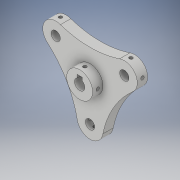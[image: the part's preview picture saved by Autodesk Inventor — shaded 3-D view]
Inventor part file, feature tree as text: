
AUTODESK INVENTOR PART (.ipt)
format: ipt  version: 2019 (Build 230136000, 136)  size: 258,048 bytes
history: native  units: mm
features: plane x10, sketch x9, hole x6, extrude x4, mirror x2, projected_geometry x2, other x1
ambient origin geometry x8: Origin, YZ Plane, XZ Plane, XY Plane, X Axis, Y Axis, Z Axis, Center Point
bodies: Body1 (feature_tree)
feature tree (34):
  other  "實體1"
  extrude  "擠出1"  Depth=109.5mm
  extrude  "擠出2"  Depth=43.5mm
  extrude  "擠出3"  Depth=76.5mm
  extrude  "擠出4"  Depth=25.0mm
  plane  "工作平面1"
  plane  "工作平面2"
  sketch  "草圖5"
  sketch  "草圖6"
  hole  "孔1"  [1 undecoded]
  hole  "孔2"  [1 undecoded]
  plane  "工作平面4"
  plane  "工作平面9"
  plane  "工作平面11"
  plane  "工作平面12"
  sketch  "草圖10"
  sketch  "草圖11"
  hole  "孔3"  [1 undecoded]
  hole  "孔4"  [1 undecoded]
  mirror  "鏡射1"
  hole  "孔5"  [1 undecoded]
  mirror  "鏡射2"
  plane  "工作平面14"
  plane  "工作平面15"
  hole  "孔7"  [1 undecoded]
  sketch  "草圖1"
  projected_geometry  "投影迴路1"
  sketch  "草圖3"
  sketch  "草圖4"
  projected_geometry  "投影迴路2"
  plane  "工作平面10"
  sketch  "草圖14"
  plane  "工作平面13"
  sketch  "草圖16"
note: 6 required parameter values undecoded (feature->parameter linkage not recoverable at this tier; creation-order binding heuristic only, values carry confidence <= 0.55)
